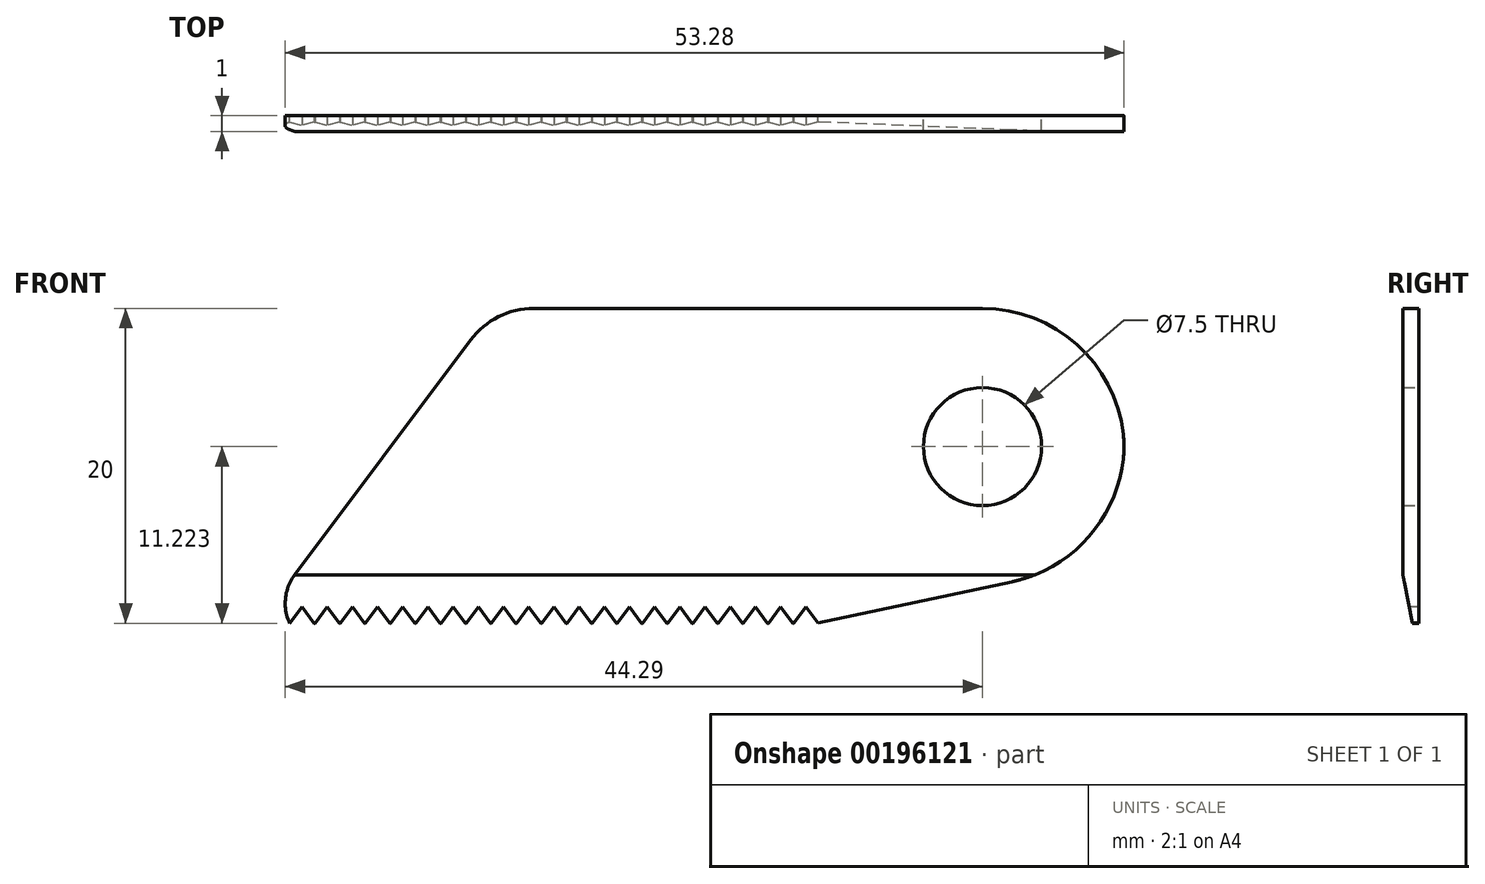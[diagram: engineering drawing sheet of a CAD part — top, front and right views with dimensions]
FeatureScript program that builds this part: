
annotation { "Feature Type Name" : "Feature", "Feature Type Description" : "" }
export const myFeature = defineFeature(function(context is Context, id is Id, definition is map)
    precondition{}
    {
        {
            var Q0;
            Q0=qCreatedBy(makeId("Front.planeOp"),FACE);
            var sketch = newSketch(context, id + "F0", { "sketchPlane" : qUnion([Q0])});
            skLineSegment(sketch, "E0.bottom", {"start": v(7.94, -10) * mm, "end": v(-27.5, -10) * mm});
            skLineSegment(sketch, "E0.top", {"start": v(18.5, 10) * mm, "end": v(-12.5, 10) * mm});
            skPoint(sketch, "E0.middle", {"position": v(0, 0) * mm});
            skLineSegment(sketch, "E1", {"start": v(-27.5, -10) * mm, "end": v(-12.5, 10) * mm});
            skLineSegment(sketch, "E2", {"start": v(7.94, -10) * mm, "end": v(20.37, -7.36) * mm});
            skPoint(sketch, "E0.right.end.orphan", {"position": v(-27.5, 10) * mm});
            skPoint(sketch, "E3.orphan", {"position": v(27.5, -10) * mm});
            skPoint(sketch, "E4.visualSharp", {"position": v(27.5, 10) * mm});
            skArc(sketch, "E4.filletArc", {"start": v(27.44, 2) * mm, "mid": v(24.5, 7.7) * mm, "end": v(18.5, 10) * mm});
            skPoint(sketch, "E5.visualSharp", {"position": v(27.5, -5.84) * mm});
            skArc(sketch, "E5.filletArc", {"start": v(20.37, -7.36) * mm, "mid": v(25.17, -4.6) * mm, "end": v(27.44, 0.44) * mm});
            skPoint(sketch, "E6.visualSharp", {"position": v(27.5, 1.22) * mm});
            skArc(sketch, "E6.filletArc", {"start": v(27.44, 0.44) * mm, "mid": v(27.49, 1.22) * mm, "end": v(27.44, 2) * mm});
            skLineSegment(sketch, "E7", {"start": v(18.5, 10) * mm, "end": v(18.5, 0.5) * mm, "construction": true});
            skLineSegment(sketch, "E8", {"start": v(27.5, 1.22) * mm, "end": v(16.2, 1.22) * mm, "construction": true});
            skCircle(sketch, "E9", {"center": v(18.5, 1.22) * mm, "radius": 3.75 * mm});
            skSolve(sketch);
        }
        {
            var Q0;
            Q0 = qSketchRegion(id + "F0", true);
            extrude(context, id + "F1", {"entities" : qUnion([Q0]), "depth" : 1 * mm});
        }
        {
            var Q0;
            Q0=makeQuery(id+"F1.opExtrude","SWEPT_EDGE",EDGE,{"disambiguationData":[OSD([sQuery(id+"F0.wireOp",EDGE,"E0.top"),sQuery(id+"F0.wireOp",EDGE,"E1")])]});
            fillet(context, id + "F2", {"entities" : qUnion([Q0]), "radius" : 5 * mm, "tangentPropagation" : true, "allowEdgeOverflow" : false});
        }
        {
            var Q0;
            Q0=makeQuery(id+"F1.opExtrude","SWEPT_EDGE",EDGE,{"disambiguationData":[OSD([sQuery(id+"F0.wireOp",EDGE,"E0.bottom"),sQuery(id+"F0.wireOp",EDGE,"E1")])]});
            fillet(context, id + "F3", {"entities" : qUnion([Q0]), "radius" : 1 * mm, "tangentPropagation" : true, "allowEdgeOverflow" : false});
        }
        {
            var Q0;
            Q0=makeQuery(id+"F1.opExtrude","CAP_FACE",FACE,{"disambiguationData":[OSD([sQuery(id+"F0.wireOp",EDGE,"E0.bottom"),sQuery(id+"F0.wireOp",EDGE,"E0.top"),sQuery(id+"F0.wireOp",EDGE,"E1"),sQuery(id+"F0.wireOp",EDGE,"E2"),sQuery(id+"F0.wireOp",EDGE,"E4.filletArc"),sQuery(id+"F0.wireOp",EDGE,"E5.filletArc"),sQuery(id+"F0.wireOp",EDGE,"E6.filletArc"),sQuery(id+"F0.wireOp",EDGE,"E9")])],"isStart":false});
            var sketch = newSketch(context, id + "F4", { "sketchPlane" : qUnion([Q0])});
            skLineSegment(sketch, "E10", {"start": v(-25.5, -10) * mm, "end": v(-24.72, -8.96) * mm});
            skLineSegment(sketch, "E11", {"start": v(-24.72, -8.96) * mm, "end": v(-24.72, -10) * mm, "construction": true});
            skLineSegment(sketch, "E12.MirrorCS", {"start": v(-23.94, -10) * mm, "end": v(-24.72, -8.96) * mm});
            skLineSegment(sketch, "E13.1.0.0", {"start": v(-23.9, -10) * mm, "end": v(-23.12, -8.96) * mm});
            skLineSegment(sketch, "E13.1.0.1", {"start": v(-22.34, -10) * mm, "end": v(-23.12, -8.96) * mm});
            skLineSegment(sketch, "E13.2.0.0", {"start": v(-22.3, -10) * mm, "end": v(-21.52, -8.96) * mm});
            skLineSegment(sketch, "E13.2.0.1", {"start": v(-20.74, -10) * mm, "end": v(-21.52, -8.96) * mm});
            skLineSegment(sketch, "E13.3.0.0", {"start": v(-20.7, -10) * mm, "end": v(-19.92, -8.96) * mm});
            skLineSegment(sketch, "E13.3.0.1", {"start": v(-19.14, -10) * mm, "end": v(-19.92, -8.96) * mm});
            skLineSegment(sketch, "E13.4.0.0", {"start": v(-19.1, -10) * mm, "end": v(-18.32, -8.96) * mm});
            skLineSegment(sketch, "E13.4.0.1", {"start": v(-17.54, -10) * mm, "end": v(-18.32, -8.96) * mm});
            skLineSegment(sketch, "E13.5.0.0", {"start": v(-17.5, -10) * mm, "end": v(-16.72, -8.96) * mm});
            skLineSegment(sketch, "E13.5.0.1", {"start": v(-15.94, -10) * mm, "end": v(-16.72, -8.96) * mm});
            skLineSegment(sketch, "E13.6.0.0", {"start": v(-15.9, -10) * mm, "end": v(-15.12, -8.96) * mm});
            skLineSegment(sketch, "E13.6.0.1", {"start": v(-14.34, -10) * mm, "end": v(-15.12, -8.96) * mm});
            skLineSegment(sketch, "E13.7.0.0", {"start": v(-14.3, -10) * mm, "end": v(-13.52, -8.96) * mm});
            skLineSegment(sketch, "E13.7.0.1", {"start": v(-12.74, -10) * mm, "end": v(-13.52, -8.96) * mm});
            skLineSegment(sketch, "E13.8.0.0", {"start": v(-12.7, -10) * mm, "end": v(-11.92, -8.96) * mm});
            skLineSegment(sketch, "E13.8.0.1", {"start": v(-11.14, -10) * mm, "end": v(-11.92, -8.96) * mm});
            skLineSegment(sketch, "E13.9.0.0", {"start": v(-11.1, -10) * mm, "end": v(-10.32, -8.96) * mm});
            skLineSegment(sketch, "E13.9.0.1", {"start": v(-9.54, -10) * mm, "end": v(-10.32, -8.96) * mm});
            skLineSegment(sketch, "E13.10.0.0", {"start": v(-9.5, -10) * mm, "end": v(-8.72, -8.96) * mm});
            skLineSegment(sketch, "E13.10.0.1", {"start": v(-7.94, -10) * mm, "end": v(-8.72, -8.96) * mm});
            skLineSegment(sketch, "E13.11.0.0", {"start": v(-7.9, -10) * mm, "end": v(-7.12, -8.96) * mm});
            skLineSegment(sketch, "E13.11.0.1", {"start": v(-6.34, -10) * mm, "end": v(-7.12, -8.96) * mm});
            skLineSegment(sketch, "E13.12.0.0", {"start": v(-6.3, -10) * mm, "end": v(-5.52, -8.96) * mm});
            skLineSegment(sketch, "E13.12.0.1", {"start": v(-4.74, -10) * mm, "end": v(-5.52, -8.96) * mm});
            skLineSegment(sketch, "E13.13.0.0", {"start": v(-4.7, -10) * mm, "end": v(-3.92, -8.96) * mm});
            skLineSegment(sketch, "E13.13.0.1", {"start": v(-3.14, -10) * mm, "end": v(-3.92, -8.96) * mm});
            skLineSegment(sketch, "E13.14.0.0", {"start": v(-3.1, -10) * mm, "end": v(-2.32, -8.96) * mm});
            skLineSegment(sketch, "E13.14.0.1", {"start": v(-1.54, -10) * mm, "end": v(-2.32, -8.96) * mm});
            skLineSegment(sketch, "E13.15.0.0", {"start": v(-1.5, -10) * mm, "end": v(-0.72, -8.96) * mm});
            skLineSegment(sketch, "E13.15.0.1", {"start": v(0.06, -10) * mm, "end": v(-0.72, -8.96) * mm});
            skLineSegment(sketch, "E13.16.0.0", {"start": v(0.1, -10) * mm, "end": v(0.88, -8.96) * mm});
            skLineSegment(sketch, "E13.16.0.1", {"start": v(1.66, -10) * mm, "end": v(0.88, -8.96) * mm});
            skLineSegment(sketch, "E13.17.0.0", {"start": v(1.7, -10) * mm, "end": v(2.48, -8.96) * mm});
            skLineSegment(sketch, "E13.17.0.1", {"start": v(3.26, -10) * mm, "end": v(2.48, -8.96) * mm});
            skLineSegment(sketch, "E13.18.0.0", {"start": v(3.3, -10) * mm, "end": v(4.08, -8.96) * mm});
            skLineSegment(sketch, "E13.18.0.1", {"start": v(4.86, -10) * mm, "end": v(4.08, -8.96) * mm});
            skLineSegment(sketch, "E13.19.0.0", {"start": v(4.9, -10) * mm, "end": v(5.68, -8.96) * mm});
            skLineSegment(sketch, "E13.19.0.1", {"start": v(6.46, -10) * mm, "end": v(5.68, -8.96) * mm});
            skLineSegment(sketch, "E13.20.0.0", {"start": v(6.5, -10) * mm, "end": v(7.28, -8.96) * mm});
            skLineSegment(sketch, "E13.20.0.1", {"start": v(8.06, -10) * mm, "end": v(7.28, -8.96) * mm});
            skLineSegment(sketch, "E13.direction1", {"start": v(-25.5, -10) * mm, "end": v(-23.9, -10) * mm, "construction": true});
            skLineSegment(sketch, "E14", {"start": v(-25.5, -10) * mm, "end": v(-25.5, -14.03) * mm});
            skLineSegment(sketch, "E15", {"start": v(-25.5, -14.03) * mm, "end": v(7.94, -14.03) * mm});
            skLineSegment(sketch, "E16", {"start": v(7.94, -14.03) * mm, "end": v(8.06, -10) * mm});
            skLineSegment(sketch, "E17", {"start": v(6.5, -10) * mm, "end": v(6.46, -10) * mm});
            skLineSegment(sketch, "E18", {"start": v(4.9, -10) * mm, "end": v(4.86, -10) * mm});
            skLineSegment(sketch, "E19", {"start": v(3.3, -10) * mm, "end": v(3.26, -10) * mm});
            skLineSegment(sketch, "E20", {"start": v(0.1, -10) * mm, "end": v(0.06, -10) * mm});
            skLineSegment(sketch, "E21", {"start": v(-1.5, -10) * mm, "end": v(-1.54, -10) * mm});
            skLineSegment(sketch, "E22", {"start": v(-3.1, -10) * mm, "end": v(-3.14, -10) * mm});
            skLineSegment(sketch, "E23", {"start": v(-4.7, -10) * mm, "end": v(-4.74, -10) * mm});
            skLineSegment(sketch, "E24", {"start": v(-6.3, -10) * mm, "end": v(-6.34, -10) * mm});
            skLineSegment(sketch, "E25", {"start": v(-7.9, -10) * mm, "end": v(-7.94, -10) * mm});
            skLineSegment(sketch, "E26", {"start": v(-9.5, -10) * mm, "end": v(-9.54, -10) * mm});
            skLineSegment(sketch, "E27", {"start": v(-11.1, -10) * mm, "end": v(-11.14, -10) * mm});
            skLineSegment(sketch, "E28", {"start": v(-12.7, -10) * mm, "end": v(-12.74, -10) * mm});
            skLineSegment(sketch, "E29", {"start": v(-14.3, -10) * mm, "end": v(-14.34, -10) * mm});
            skLineSegment(sketch, "E30", {"start": v(-15.9, -10) * mm, "end": v(-15.94, -10) * mm});
            skLineSegment(sketch, "E31", {"start": v(-17.5, -10) * mm, "end": v(-17.54, -10) * mm});
            skLineSegment(sketch, "E32", {"start": v(-19.1, -10) * mm, "end": v(-19.14, -10) * mm});
            skLineSegment(sketch, "E33", {"start": v(-20.7, -10) * mm, "end": v(-20.74, -10) * mm});
            skLineSegment(sketch, "E34", {"start": v(-22.3, -10) * mm, "end": v(-22.34, -10) * mm});
            skLineSegment(sketch, "E35", {"start": v(-23.9, -10) * mm, "end": v(-23.94, -10) * mm});
            skLineSegment(sketch, "E36", {"start": v(1.66, -10) * mm, "end": v(1.7, -10) * mm});
            skSolve(sketch);
        }
        {
            var Q0;
            Q0 = qSketchRegion(id + "F4", true);
            extrude(context, id + "F5", {"entities" : qUnion([Q0]), "operationType" : NewBodyOperationType.REMOVE, "oppositeDirection" : true, "depth" : 25 * mm});
        }
        {
            var Q0;
            Q0=makeQuery(id+"F1.opExtrude","CAP_FACE",FACE,{"disambiguationData":[OSD([sQuery(id+"F0.wireOp",EDGE,"E0.bottom"),sQuery(id+"F0.wireOp",EDGE,"E0.top"),sQuery(id+"F0.wireOp",EDGE,"E1"),sQuery(id+"F0.wireOp",EDGE,"E2"),sQuery(id+"F0.wireOp",EDGE,"E4.filletArc"),sQuery(id+"F0.wireOp",EDGE,"E5.filletArc"),sQuery(id+"F0.wireOp",EDGE,"E6.filletArc"),sQuery(id+"F0.wireOp",EDGE,"E9")])],"isStart":false});
            var sketch = newSketch(context, id + "F6", { "sketchPlane" : qUnion([Q0])});
            skLineSegment(sketch, "E37", {"start": v(-25.5, -10) * mm, "end": v(-26.3, -8.4) * mm});
            skLineSegment(sketch, "E38", {"start": v(-26.3, -8.4) * mm, "end": v(-30.44, -7.87) * mm});
            skLineSegment(sketch, "E39", {"start": v(-30.44, -7.87) * mm, "end": v(-26.66, -14.28) * mm});
            skLineSegment(sketch, "E40", {"start": v(-26.66, -14.28) * mm, "end": v(-25.5, -10) * mm});
            skSolve(sketch);
        }
        {
            var Q0;
            Q0 = qSketchRegion(id + "F6", true);
            extrude(context, id + "F7", {"entities" : qUnion([Q0]), "operationType" : NewBodyOperationType.REMOVE, "oppositeDirection" : true, "depth" : 25 * mm});
        }
        {
            var Q0;
            {var subQ0=sQuery(id+"F0.wireOp",EDGE,"E1");var subQ1=sQuery(id+"F0.wireOp",EDGE,"E0.bottom");Q0=makeQuery(id+"F7.boolean.opBoolean","MERGE",EDGE,{"derivedFrom":[makeQuery(id+"F3.opFillet","BLEND_EDGE",EDGE,{"blendedFrom":[makeQuery(id+"F1.opExtrude","SWEPT_EDGE",EDGE,{"disambiguationData":[OSD([subQ1,subQ0])]}),makeQuery(id+"F1.opExtrude","SWEPT_FACE",FACE,{"disambiguationData":[OSD([subQ0])]})],"blendedInto":[makeQuery(id+"F1.opExtrude","SWEPT_FACE",FACE,{"disambiguationData":[OSD([subQ0])]})]}),makeQuery(id+"F7.opExtrude","SWEPT_EDGE",EDGE,{"disambiguationData":[OSD([subQ1,sQuery(id+"F0.wireOp",EDGE,"E0.top"),subQ0,sQuery(id+"F0.wireOp",EDGE,"E2"),sQuery(id+"F0.wireOp",EDGE,"E4.filletArc"),sQuery(id+"F0.wireOp",EDGE,"E5.filletArc"),sQuery(id+"F0.wireOp",EDGE,"E6.filletArc"),sQuery(id+"F0.wireOp",EDGE,"E9"),sQuery(id+"F6.wireOp",EDGE,"E37"),sQuery(id+"F6.wireOp",EDGE,"E38")])]})]});}
            fillet(context, id + "F8", {"entities" : qUnion([Q0]), "radius" : 3 * mm, "tangentPropagation" : true, "allowEdgeOverflow" : false});
        }
        {
            var Q0;
            Q0=qCreatedBy(makeId("Right.planeOp"),FACE);
            var sketch = newSketch(context, id + "F9", { "sketchPlane" : qUnion([Q0])});
            skLineSegment(sketch, "E41", {"start": v(-0.4, -10) * mm, "end": v(-1, -6.92) * mm});
            skLineSegment(sketch, "E42", {"start": v(-1, -6.92) * mm, "end": v(-2.56, -6.92) * mm});
            skLineSegment(sketch, "E43", {"start": v(-2.56, -6.92) * mm, "end": v(-2.56, -10.82) * mm});
            skLineSegment(sketch, "E44", {"start": v(-2.56, -10.82) * mm, "end": v(-0.4, -10) * mm});
            skSolve(sketch);
        }
        {
            var Q0;
            Q0 = qSketchRegion(id + "F9", true);
            extrude(context, id + "F10", {"entities" : qUnion([Q0]), "operationType" : NewBodyOperationType.REMOVE, "oppositeDirection" : true, "depth" : 30 * mm, "hasSecondDirection" : true, "secondDirectionOppositeDirection" : false, "secondDirectionDepth" : 25 * mm});
        }
    });
